# Revit family: Vertical_Air_Handler-V_Series-Hot_Water_Coil+Chilled_Water_Coil
name_source: partatom
category: Mechanical Equipment
units: mm (PartAtom-declared; Revit-internal decimal feet)

## family parameters
Always vertical = Yes
Classification = None
Cut with Voids When Loaded = No
OmniClass Number = 23.75.70.00
OmniClass Title = HVAC Distribution Devices
Part Type = Normal
Room Calculation Point = No
Round Connector Dimension = Use Diameter
Shared = No
Work Plane-Based = No

## types (3) — shared parameters
Apparent Load = 208 VA
Assembly Code = D3040100
C LUT Cooling = Size-RMB
C LUT Heating = Size-HM
Chilled Water Coil Connection Diameter = 1"
Default Elevation = 0' - 0"
Description = Vertical Fan Coil
Drain Connection Diameter = 1"
Finish = Metal - Unico - Silver
Frequency = 60 Hz
Hot Water Coil Connection Diameter = 1"
Instruction Sheet Link = https://www.unicosystem.com
Keynote = 23 30 00
Load Classification = HVAC
Manufacturer = Unico, Inc.
Manufacturer Fax Number = 314-457-9000
Number of Poles = 1
Performance URL = https://www.unicosystem.com
Power Factor = 1
Product Page URL = https://shop.unicosystem.com
URL = https://www.unicosystem.com
Version = 2020 - v1.0a
Video Link = https://www.youtube.com
Warranty URL = https://www.unicosystem.com

## per-type parameters (varying)
| type | Constraints | Depth | Height | Return Connection Height | Return Connection Width | Width |
| V2430B-1EC2CH | 2 | 1' - 8" | 3' - 6 3/32" | 1' - 6" | 1' - 6" | 1' - 8" |
| V3036B-1EC2CH | 3 | 2' - 0" | 3' - 6" | 1' - 10" | 1' - 6" | 1' - 8" |
| V3642B-1EC2CH | 4 | 2' - 1" | 3' - 8" | 1' - 11" | 1' - 9 1/2" | 1' - 11 13/16" |

note: column(s) folded — value = type name in every type: Model

## geometry (parser evidence)
native form markers: Sweep x14
no freeform markers — native parametric forms only
